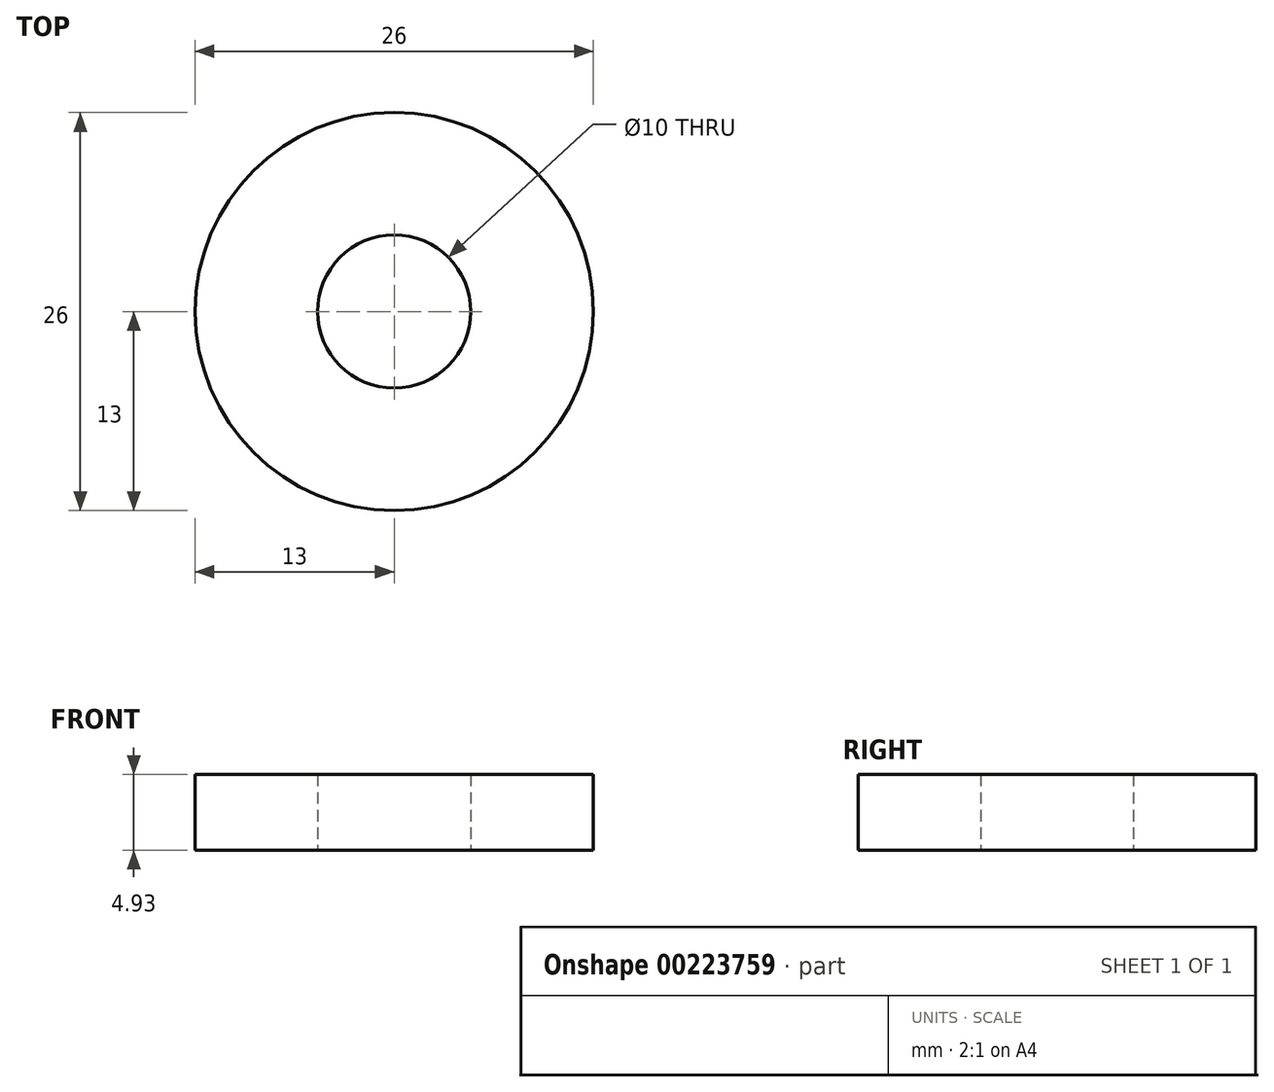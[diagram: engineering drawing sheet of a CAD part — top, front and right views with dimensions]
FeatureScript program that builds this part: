
annotation { "Feature Type Name" : "Feature", "Feature Type Description" : "" }
export const myFeature = defineFeature(function(context is Context, id is Id, definition is map)
    precondition{}
    {
        {
            var Q0;
            Q0=qCreatedBy(makeId("Top.planeOp"),FACE);
            var sketch = newSketch(context, id + "F0", { "sketchPlane" : qUnion([Q0])});
            skCircle(sketch, "E0", {"center": v(0, 0) * mm, "radius": 5 * mm});
            skCircle(sketch, "E1", {"center": v(0, 0) * mm, "radius": 13 * mm});
            skSolve(sketch);
        }
        {
            var Q0;
            Q0=makeQuery(id+"F0.imprint","IMPRINT",FACE,{"disambiguationData":[TD([[makeQuery(id+"F0.imprint","IMPRINT",EDGE,{"derivedFrom":sQuery(id+"F0.wireOp",EDGE,"E0")}),-1.0]])]});
            extrude(context, id + "F1", {"entities" : qUnion([Q0]), "depth" : 4.93 * mm});
        }
    });
